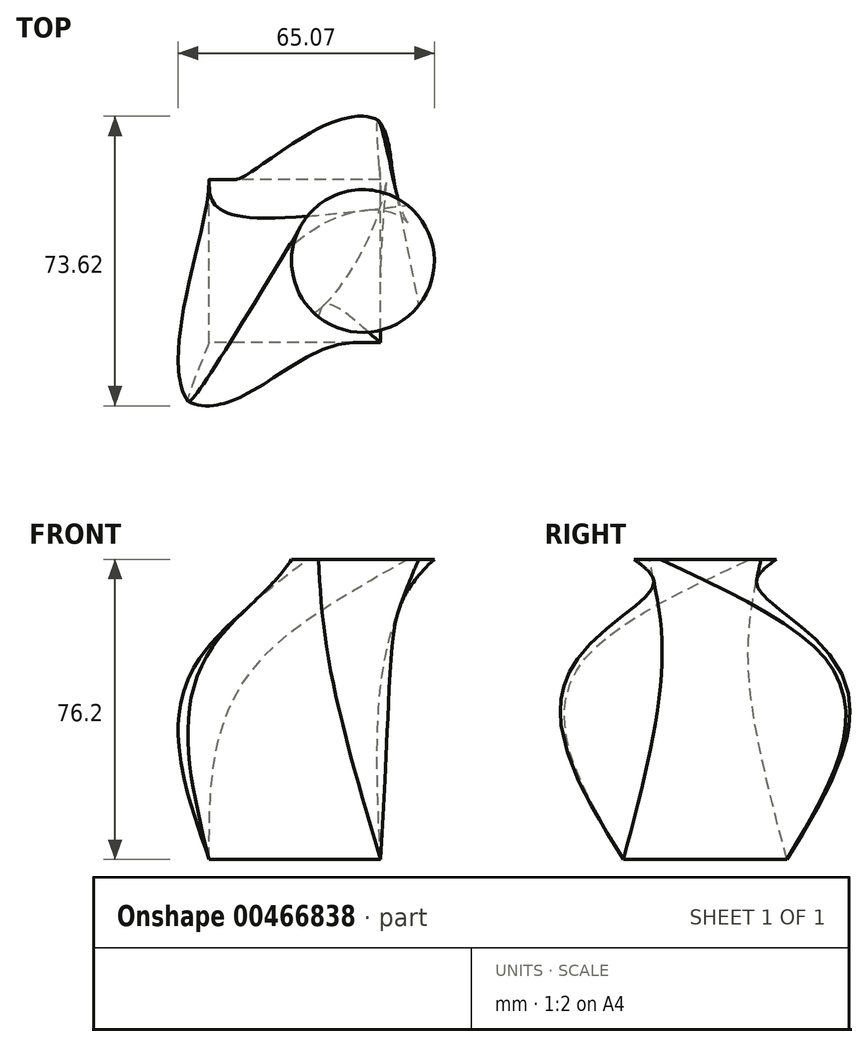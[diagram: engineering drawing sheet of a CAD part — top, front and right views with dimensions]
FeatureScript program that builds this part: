
annotation { "Feature Type Name" : "Feature", "Feature Type Description" : "" }
export const myFeature = defineFeature(function(context is Context, id is Id, definition is map)
    precondition{}
    {
        {
            var Q0;
            Q0=qCreatedBy(makeId("Top.planeOp"),FACE);
            cPlane(context, id + "F0", {"entities" : qUnion([Q0]), "cplaneType" : CPlaneType.OFFSET, "offset" : 50.8 * mm, "width" : 152.4 * mm, "height" : 152.4 * mm});
        }
        {
            var Q0;
            Q0=qCreatedBy(id+"F0.planeOp",FACE);
            var sketch = newSketch(context, id + "F1", { "sketchPlane" : qUnion([Q0])});
            skEllipse(sketch, "E0", {"center": v(0, 0) * mm, "majorRadius": 38.43 * mm, "minorRadius": 13.32 * mm, "majorAxis": v(0.57, 0.82)});
            skSolve(sketch);
        }
        {
            var Q0;
            Q0=qCreatedBy(makeId("Top.planeOp"),FACE);
            var sketch = newSketch(context, id + "F2", { "sketchPlane" : qUnion([Q0])});
            skLineSegment(sketch, "E1.bottom", {"start": v(21.74, -20.75) * mm, "end": v(-21.74, -20.75) * mm});
            skLineSegment(sketch, "E1.top", {"start": v(21.74, 20.75) * mm, "end": v(-21.74, 20.75) * mm});
            skLineSegment(sketch, "E1.left", {"start": v(21.74, -20.75) * mm, "end": v(21.74, 20.75) * mm});
            skLineSegment(sketch, "E1.right", {"start": v(-21.74, -20.75) * mm, "end": v(-21.74, 20.75) * mm});
            skPoint(sketch, "E1.middle", {"position": v(0, 0) * mm});
            skSolve(sketch);
        }
        {
            var Q0;
            Q0=qCreatedBy(id+"F0.planeOp",FACE);
            cPlane(context, id + "F3", {"entities" : qUnion([Q0]), "cplaneType" : CPlaneType.OFFSET, "offset" : 25.4 * mm, "width" : 152.4 * mm, "height" : 152.4 * mm});
        }
        {
            var Q0;
            Q0=qCreatedBy(id+"F3.planeOp",FACE);
            var sketch = newSketch(context, id + "F4", { "sketchPlane" : qUnion([Q0])});
            skCircle(sketch, "E2", {"center": v(17.3, 0) * mm, "radius": 18.14 * mm});
            skSolve(sketch);
        }
        {
            var Q0;
            Q0=makeQuery(id+"F2.imprint","IMPRINT",FACE,{"disambiguationData":[TD([[makeQuery(id+"F2.imprint","IMPRINT",EDGE,{"derivedFrom":sQuery(id+"F2.wireOp",EDGE,"E1.bottom")}),-1.0]])]});
            var Q1;
            Q1=makeQuery(id+"F1.imprint","IMPRINT",FACE,{"disambiguationData":[TD([[makeQuery(id+"F1.imprint","IMPRINT",EDGE,{"derivedFrom":sQuery(id+"F1.wireOp",EDGE,"E0")}),1.0]])]});
            var Q2;
            Q2=makeQuery(id+"F4.imprint","IMPRINT",FACE,{"disambiguationData":[TD([[makeQuery(id+"F4.imprint","IMPRINT",EDGE,{"derivedFrom":sQuery(id+"F4.wireOp",EDGE,"E2")}),1.0]])]});
            loft(context, id + "F5", {"sheetProfilesArray" : [{ "sheetProfileEntities" : qUnion([Q0]) }, { "sheetProfileEntities" : qUnion([Q1]) }, { "sheetProfileEntities" : qUnion([Q2]) }]});
        }
    });
